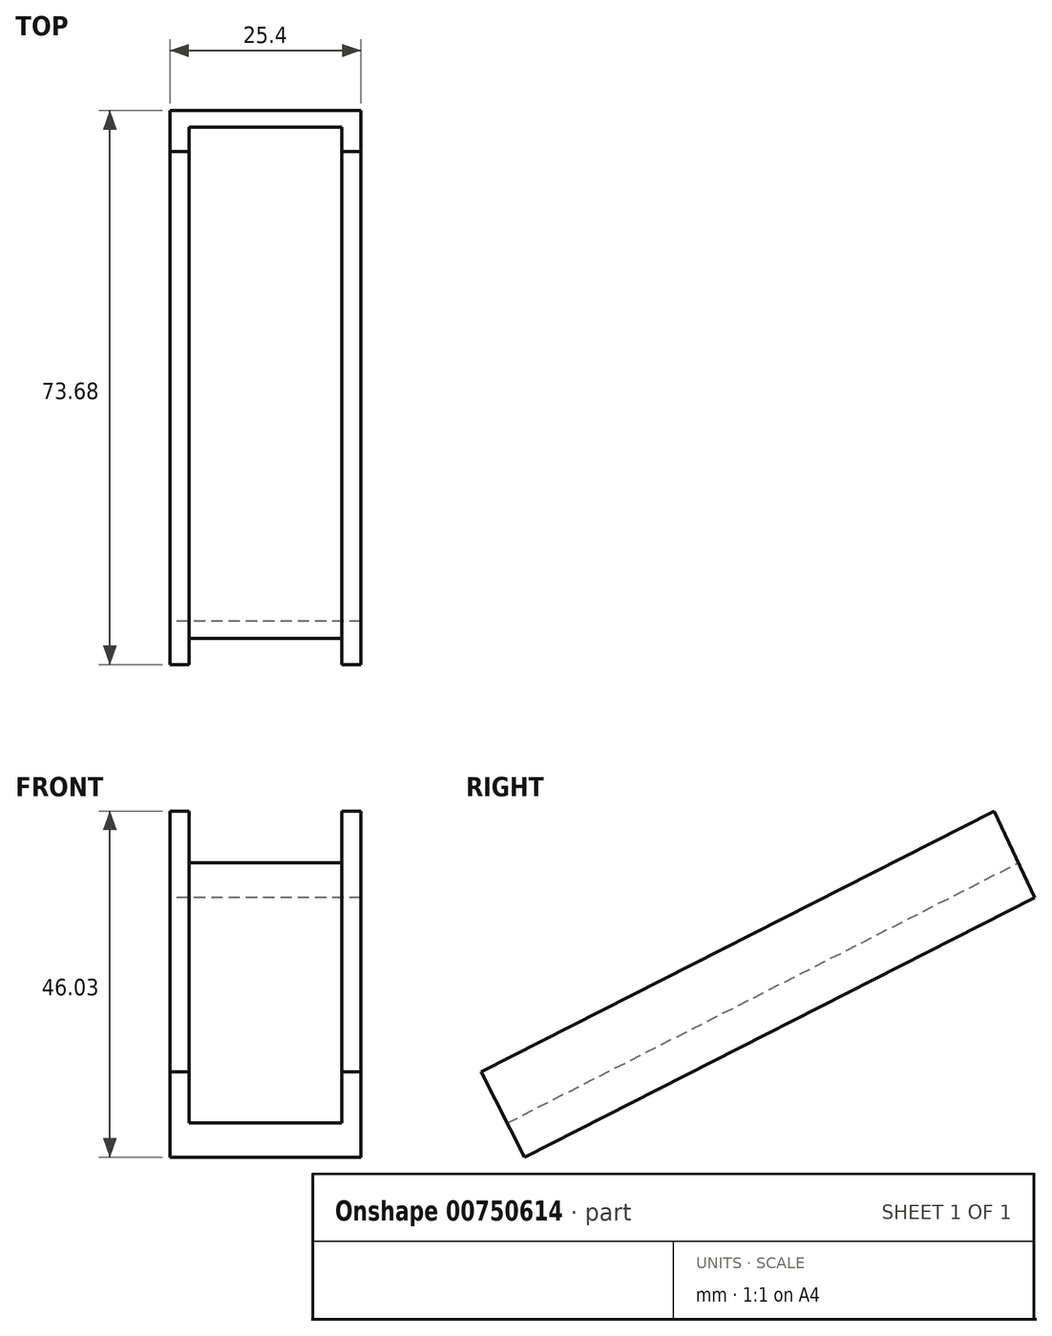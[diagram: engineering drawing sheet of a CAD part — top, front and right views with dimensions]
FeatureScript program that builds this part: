
annotation { "Feature Type Name" : "Feature", "Feature Type Description" : "" }
export const myFeature = defineFeature(function(context is Context, id is Id, definition is map)
    precondition{}
    {
        {
            var Q0;
            Q0=qCreatedBy(makeId("Right.planeOp"),FACE);
            var sketch = newSketch(context, id + "F0", { "sketchPlane" : qUnion([Q0])});
            skLineSegment(sketch, "E0", {"start": v(0, 0) * mm, "end": v(67.92, 34.55) * mm});
            skLineSegment(sketch, "E1", {"start": v(0, 0) * mm, "end": v(-5.76, 11.32) * mm});
            skLineSegment(sketch, "E2", {"start": v(-5.76, 11.32) * mm, "end": v(62.48, 46.03) * mm});
            skLineSegment(sketch, "E3", {"start": v(62.48, 46.03) * mm, "end": v(67.92, 34.55) * mm});
            skSolve(sketch);
        }
        {
            var Q0;
            Q0 = qSketchRegion(id + "F0", true);
            extrude(context, id + "F1", {"entities" : qUnion([Q0]), "depth" : 25.4 * mm, "offsetDistance" : 25.4 * mm});
        }
        {
            var Q0;
            Q0=makeQuery(id+"F1.opExtrude","SWEPT_FACE",FACE,{"disambiguationData":[OSD([sQuery(id+"F0.wireOp",EDGE,"E2")])]});
            var sketch = newSketch(context, id + "F2", { "sketchPlane" : qUnion([Q0])});
            skLineSegment(sketch, "E4", {"start": v(2.54, 0) * mm, "end": v(2.54, 76.56) * mm});
            skLineSegment(sketch, "E5", {"start": v(2.54, 76.56) * mm, "end": v(22.86, 76.56) * mm});
            skLineSegment(sketch, "E6", {"start": v(22.86, 76.56) * mm, "end": v(22.86, 0) * mm});
            skSolve(sketch);
        }
        {
            var Q0;
            Q0 = qSketchRegion(id + "F2", true);
            var Q1;
            {var subQ0=sQuery(id+"F2.wireOp",EDGE,"E4");Q1=makeQuery(id+"F2.imprint","IMPRINT",FACE,{"disambiguationData":[TD([[makeQuery(id+"F2.imprint","IMPRINT",EDGE,{"derivedFrom":subQ0}),-1.0]])]});}
            extrude(context, id + "F3", {"entities" : qUnion([Q0, Q1]), "operationType" : NewBodyOperationType.REMOVE, "oppositeDirection" : true, "depth" : 7.62 * mm, "offsetDistance" : 25.4 * mm});
        }
    });
